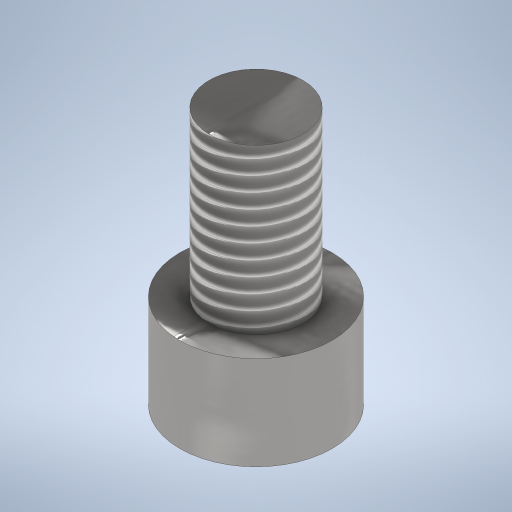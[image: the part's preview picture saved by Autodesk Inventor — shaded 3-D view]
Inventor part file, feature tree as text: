
AUTODESK INVENTOR PART (.ipt)
format: ipt  version: 2024.2 (Build 282272000, 272)  size: 314,880 bytes
history: native  units: mm
features: sketch x2, revolve x1, thread x1, extrude x1
ambient origin geometry x8: Origin, YZ Plane, XZ Plane, XY Plane, X Axis, Y Axis, Z Axis, Center Point
bodies: Solid1 (feature_tree)
feature tree (5):
  revolve  "Revolution1"  [1 undecoded]
  thread  "Thread1"  [1 undecoded]
  extrude  "Extrusion1"  [1 undecoded]
  sketch  "Sketch1"  dims[d4=90.0deg d5=15.0mm d6=0.0mm d0=0.0mm]
  sketch  "Sketch2"
note: 3 required parameter values undecoded (feature->parameter linkage not recoverable at this tier; creation-order binding heuristic only, values carry confidence <= 0.55)